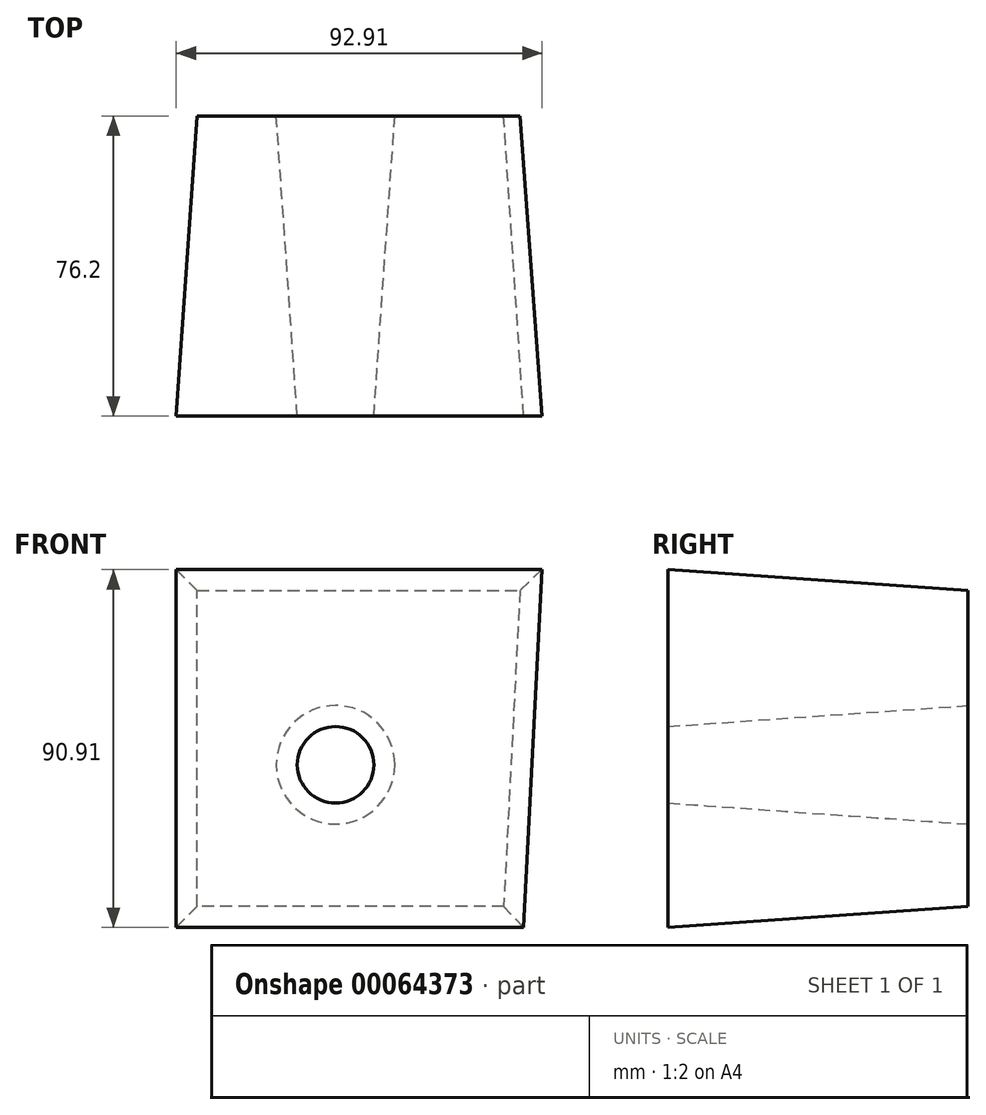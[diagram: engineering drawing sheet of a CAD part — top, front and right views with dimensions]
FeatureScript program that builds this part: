
annotation { "Feature Type Name" : "Feature", "Feature Type Description" : "" }
export const myFeature = defineFeature(function(context is Context, id is Id, definition is map)
    precondition{}
    {
        {
            var Q0;
            Q0=qCreatedBy(makeId("Front.planeOp"),FACE);
            var sketch = newSketch(context, id + "F0", { "sketchPlane" : qUnion([Q0])});
            skLineSegment(sketch, "E0", {"start": v(-50.98, 56.07) * mm, "end": v(-50.98, -24.2) * mm});
            skLineSegment(sketch, "E1", {"start": v(-50.98, -24.2) * mm, "end": v(26.87, -24.2) * mm});
            skLineSegment(sketch, "E2", {"start": v(26.87, -24.2) * mm, "end": v(31, 56.07) * mm});
            skLineSegment(sketch, "E3", {"start": v(31, 56.07) * mm, "end": v(-50.98, 56.07) * mm});
            skCircle(sketch, "E4", {"center": v(-15.84, 11.79) * mm, "radius": 15.06 * mm});
            skSolve(sketch);
        }
        {
            var Q0;
            Q0 = qSketchRegion(id + "F0", true);
            extrude(context, id + "F1", {"entities" : qUnion([Q0]), "depth" : 76.2 * mm, "hasDraft" : true, "draftAngle" : 4 * degree});
        }
    });
